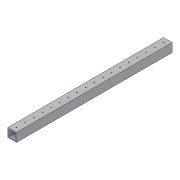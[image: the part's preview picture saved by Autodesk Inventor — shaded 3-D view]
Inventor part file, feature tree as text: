
AUTODESK INVENTOR PART (.ipt)
format: ipt  version: 2018 (Build 220112000, 112)  size: 126,464 bytes
history: native  units: in
note: dims shown in document units (in); Inventor stores cm internally (conversion verified against a paired STEP export)
features: sketch x2, extrude x1, shell x1, hole x1
ambient origin geometry x8: Origin, YZ Plane, XZ Plane, XY Plane, X Axis, Y Axis, Z Axis, Center Point
bodies: Solid1 (feature_tree)
feature tree (5):
  extrude  "Extrusion1"  Depth=1.0in
  shell  "Shell1"  Thickness=18.0in
  hole  "Hole1"  [1 undecoded]
  sketch  "Sketch1"  dims[d0=1.0in d1=1.0in d2=18.0in d3=0.0in]
  sketch  "Sketch2"  dims[d4=0.1in d5=0.5in d6=0.5in d7=14.5669in d9=1.0in d10=0.3937in d12=1.0in d14=0.1in d15=0.75in d16=0.375in d17=0.25in d18=0.5635in d19=2.0in d20=0.8108in]
note: 1 required parameter value undecoded (feature->parameter linkage not recoverable at this tier; creation-order binding heuristic only, values carry confidence <= 0.55)
